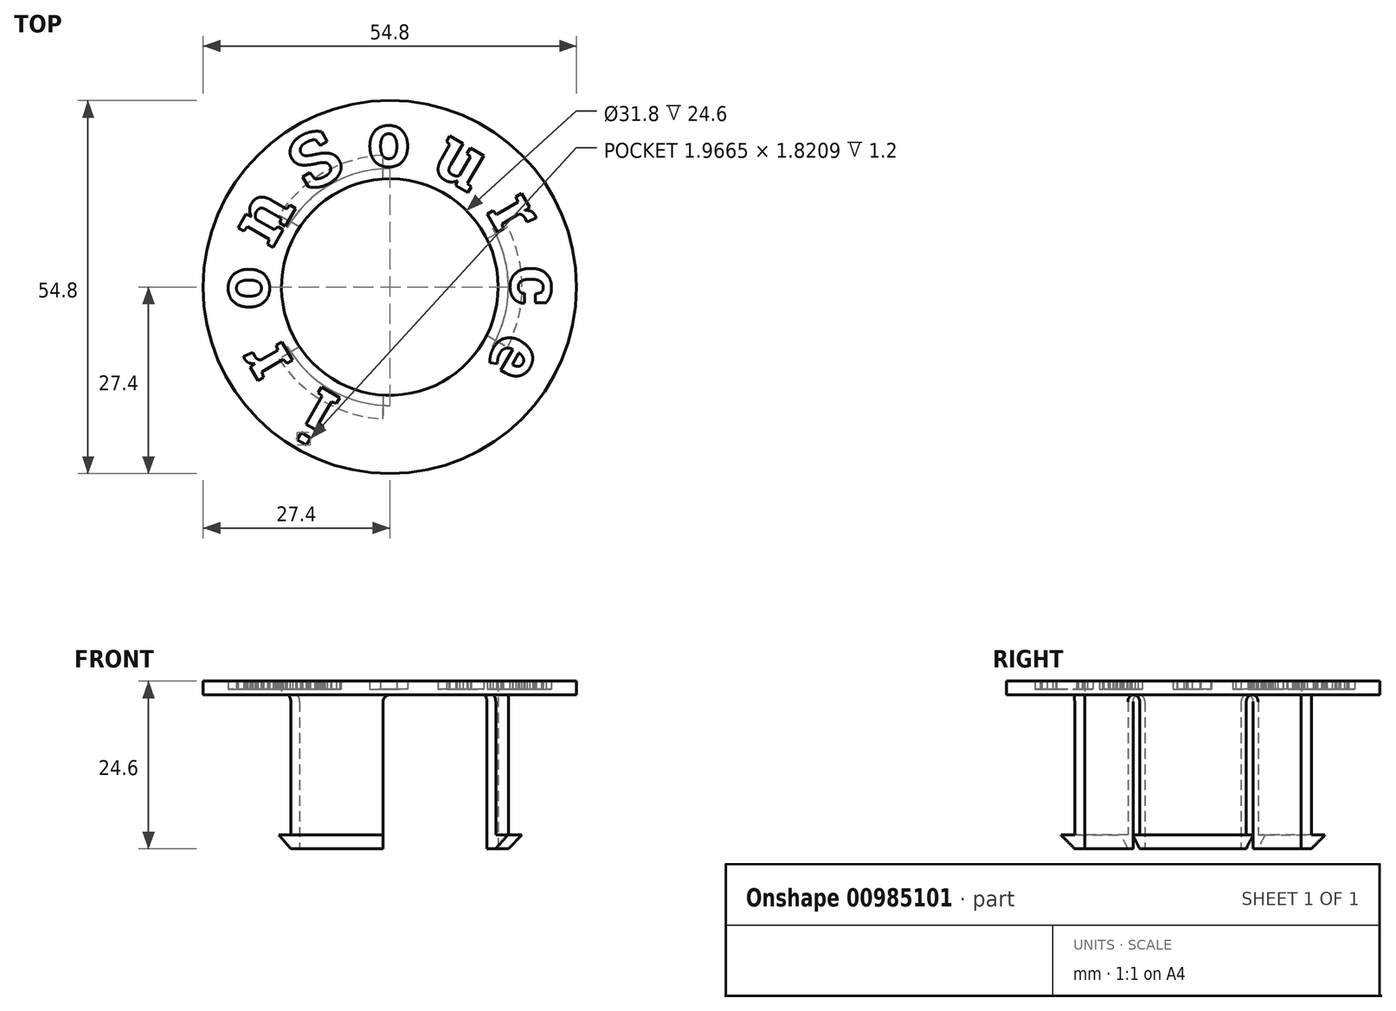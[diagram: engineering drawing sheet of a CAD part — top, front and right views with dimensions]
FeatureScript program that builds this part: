
annotation { "Feature Type Name" : "Feature", "Feature Type Description" : "" }
export const myFeature = defineFeature(function(context is Context, id is Id, definition is map)
    precondition{}
    {
        {
            var Q0;
            Q0=qCreatedBy(makeId("Top.planeOp"),FACE);
            var sketch = newSketch(context, id + "F0", { "sketchPlane" : qUnion([Q0])});
            skCircle(sketch, "E0", {"center": v(0, 0) * mm, "radius": 17.4 * mm});
            skCircle(sketch, "E1", {"center": v(0, 0) * mm, "radius": 15.9 * mm});
            skCircle(sketch, "E2", {"center": v(0, 0) * mm, "radius": 27.4 * mm});
            skLineSegment(sketch, "E3", {"start": v(0, 0) * mm, "end": v(0, 17.75) * mm, "construction": true});
            skText(sketch, "E4", { "text": "o", "fontName": "RobotoSlab-Bold.ttf"});
            skText(sketch, "E5", { "text": "u", "fontName": "RobotoSlab-Bold.ttf"});
            skText(sketch, "E6", { "text": "e", "fontName": "RobotoSlab-Bold.ttf"});
            skText(sketch, "E7", { "text": "i", "fontName": "RobotoSlab-Bold.ttf"});
            skText(sketch, "E8", { "text": "r", "fontName": "RobotoSlab-Bold.ttf"});
            skText(sketch, "E9", { "text": "c", "fontName": "RobotoSlab-Bold.ttf"});
            skText(sketch, "E10", { "text": "e", "fontName": "RobotoSlab-Bold.ttf"});
            skText(sketch, "E11", { "text": "o", "fontName": "RobotoSlab-Bold.ttf"});
            skText(sketch, "E12", { "text": "r", "fontName": "RobotoSlab-Bold.ttf"});
            skText(sketch, "E13", { "text": "n", "fontName": "RobotoSlab-Bold.ttf"});
            skLineSegment(sketch, "E14.2.0", {"start": v(0, 0) * mm, "end": v(-15.37, 8.88) * mm, "construction": true});
            skLineSegment(sketch, "E14.3.0", {"start": v(0, 0) * mm, "end": v(-17.75, 0) * mm, "construction": true});
            skLineSegment(sketch, "E14.4.0", {"start": v(0, 0) * mm, "end": v(-15.37, -8.88) * mm, "construction": true});
            skLineSegment(sketch, "E14.5.0", {"start": v(0, 0) * mm, "end": v(-8.88, -15.37) * mm, "construction": true});
            skLineSegment(sketch, "E14.6.0", {"start": v(0, 0) * mm, "end": v(0, -17.75) * mm, "construction": true});
            skLineSegment(sketch, "E14.7.0", {"start": v(0, 0) * mm, "end": v(8.87, -15.37) * mm, "construction": true});
            skLineSegment(sketch, "E14.8.0", {"start": v(0, 0) * mm, "end": v(15.37, -8.88) * mm, "construction": true});
            skLineSegment(sketch, "E14.9.0", {"start": v(0, 0) * mm, "end": v(17.75, 0) * mm, "construction": true});
            skLineSegment(sketch, "E14.10.0", {"start": v(0, 0) * mm, "end": v(15.37, 8.87) * mm, "construction": true});
            skLineSegment(sketch, "E14.11.0", {"start": v(0, 0) * mm, "end": v(8.88, 15.37) * mm, "construction": true});
            skText(sketch, "E15", { "text": "S", "fontName": "RobotoSlab-Bold.ttf"});
            skLineSegment(sketch, "E16", {"start": v(0, 0) * mm, "end": v(-8.88, 15.37) * mm, "construction": true});
            const initialGuessF0  = {"E4": [-0.00328, 0.01775, 1, 0, 0.008], "E5": [0.0057, 0.0172, 0.86603, -0.5, 0.008], "E6": [0.01692, -0.0062, -0.5, -0.86603, 0.008], "E7": [-0.0071, -0.0164, -0.86603, 0.5, 0.008], "E8": [-0.01407, -0.01114, -0.5, 0.86603, 0.008], "E9": [0.01775, 0.0031, 0, -1, 0.008], "E10": [0.01156, -0.01382, -0.86603, -0.5, 0.008], "E11": [-0.01775, -0.00328, 0, 1, 0.008], "E12": [0.01407, 0.01114, 0.5, -0.86603, 0.008], "E13": [-0.01726, 0.0056, 0.5, 0.86603, 0.008], "E15": [-0.01195, 0.0136, 0.86603, 0.5, 0.008]};
            skSetInitialGuess(sketch, initialGuessF0);
            skSolve(sketch);
        }
        {
            var Q0;
            Q0=makeQuery(id+"F0.imprint","IMPRINT",FACE,{"disambiguationData":[TD([[makeQuery(id+"F0.imprint","IMPRINT",EDGE,{"derivedFrom":sQuery(id+"F0.wireOp",EDGE,"E0")}),1.0]])]});
            var Q1;
            Q1=makeQuery(id+"F0.imprint","IMPRINT",FACE,{"disambiguationData":[TD([[makeQuery(id+"F0.imprint","IMPRINT",EDGE,{"derivedFrom":sQuery(id+"F0.wireOp",EDGE,"E4.sketch_text.stroke-0")}),-1.0]])]});
            var Q2;
            Q2=makeQuery(id+"F0.imprint","IMPRINT",FACE,{"disambiguationData":[TD([[makeQuery(id+"F0.imprint","IMPRINT",EDGE,{"derivedFrom":sQuery(id+"F0.wireOp",EDGE,"E7.sketch_text.stroke-0")}),-1.0]])]});
            var Q3;
            Q3=makeQuery(id+"F0.imprint","IMPRINT",FACE,{"disambiguationData":[TD([[makeQuery(id+"F0.imprint","IMPRINT",EDGE,{"derivedFrom":sQuery(id+"F0.wireOp",EDGE,"E11.sketch_text.stroke-10")}),1.0]])]});
            var Q4;
            Q4=makeQuery(id+"F0.imprint","IMPRINT",FACE,{"disambiguationData":[TD([[makeQuery(id+"F0.imprint","IMPRINT",EDGE,{"derivedFrom":sQuery(id+"F0.wireOp",EDGE,"E9.sketch_text.stroke-0")}),-1.0]])]});
            var Q5;
            Q5=makeQuery(id+"F0.imprint","IMPRINT",FACE,{"disambiguationData":[TD([[makeQuery(id+"F0.imprint","IMPRINT",EDGE,{"derivedFrom":sQuery(id+"F0.wireOp",EDGE,"E10.sketch_text.stroke-0")}),-1.0]])]});
            var Q6;
            Q6=makeQuery(id+"F0.imprint","IMPRINT",FACE,{"disambiguationData":[TD([[makeQuery(id+"F0.imprint","IMPRINT",EDGE,{"derivedFrom":sQuery(id+"F0.wireOp",EDGE,"E6.sketch_text.stroke-0")}),-1.0]])]});
            var Q7;
            Q7=makeQuery(id+"F0.imprint","IMPRINT",FACE,{"disambiguationData":[TD([[makeQuery(id+"F0.imprint","IMPRINT",EDGE,{"derivedFrom":sQuery(id+"F0.wireOp",EDGE,"E12.sketch_text.stroke-0")}),-1.0]])]});
            var Q8;
            Q8=makeQuery(id+"F0.imprint","IMPRINT",FACE,{"disambiguationData":[TD([[makeQuery(id+"F0.imprint","IMPRINT",EDGE,{"derivedFrom":sQuery(id+"F0.wireOp",EDGE,"E5.sketch_text.stroke-0")}),-1.0]])]});
            var Q9;
            Q9=makeQuery(id+"F0.imprint","IMPRINT",FACE,{"disambiguationData":[TD([[makeQuery(id+"F0.imprint","IMPRINT",EDGE,{"derivedFrom":sQuery(id+"F0.wireOp",EDGE,"E0")}),-1.0]])]});
            var Q10;
            Q10=makeQuery(id+"F0.imprint","IMPRINT",FACE,{"disambiguationData":[TD([[makeQuery(id+"F0.imprint","IMPRINT",EDGE,{"derivedFrom":sQuery(id+"F0.wireOp",EDGE,"E5.sketch_text.stroke-10")}),1.0]])]});
            var Q11;
            Q11=makeQuery(id+"F0.imprint","IMPRINT",FACE,{"disambiguationData":[TD([[makeQuery(id+"F0.imprint","IMPRINT",EDGE,{"derivedFrom":sQuery(id+"F0.wireOp",EDGE,"E13.sketch_text.stroke-0")}),-1.0]])]});
            var Q12;
            Q12=makeQuery(id+"F0.imprint","IMPRINT",FACE,{"disambiguationData":[TD([[makeQuery(id+"F0.imprint","IMPRINT",EDGE,{"derivedFrom":sQuery(id+"F0.wireOp",EDGE,"E8.sketch_text.stroke-0")}),-1.0]])]});
            var Q13;
            Q13=makeQuery(id+"F0.imprint","IMPRINT",FACE,{"disambiguationData":[TD([[makeQuery(id+"F0.imprint","IMPRINT",EDGE,{"derivedFrom":sQuery(id+"F0.wireOp",EDGE,"E11.sketch_text.stroke-0")}),-1.0]])]});
            var Q14;
            Q14=makeQuery(id+"F0.imprint","IMPRINT",FACE,{"disambiguationData":[TD([[makeQuery(id+"F0.imprint","IMPRINT",EDGE,{"derivedFrom":sQuery(id+"F0.wireOp",EDGE,"E7.sketch_text.stroke-10")}),-1.0]])]});
            var Q15;
            Q15=makeQuery(id+"F0.imprint","IMPRINT",FACE,{"disambiguationData":[TD([[makeQuery(id+"F0.imprint","IMPRINT",EDGE,{"derivedFrom":sQuery(id+"F0.wireOp",EDGE,"E10.sketch_text.stroke-17")}),1.0]])]});
            var Q16;
            Q16=makeQuery(id+"F0.imprint","IMPRINT",FACE,{"disambiguationData":[TD([[makeQuery(id+"F0.imprint","IMPRINT",EDGE,{"derivedFrom":sQuery(id+"F0.wireOp",EDGE,"E15.sketch_text.stroke-0")}),-1.0]])]});
            var Q17;
            Q17=makeQuery(id+"F0.imprint","IMPRINT",FACE,{"disambiguationData":[TD([[makeQuery(id+"F0.imprint","IMPRINT",EDGE,{"derivedFrom":sQuery(id+"F0.wireOp",EDGE,"E4.sketch_text.stroke-10")}),1.0]])]});
            var Q18;
            Q18=makeQuery(id+"F0.imprint","IMPRINT",FACE,{"disambiguationData":[TD([[makeQuery(id+"F0.imprint","IMPRINT",EDGE,{"derivedFrom":sQuery(id+"F0.wireOp",EDGE,"E6.sketch_text.stroke-17")}),1.0]])]});
            extrude(context, id + "F1", {"entities" : qUnion([Q0, Q1, Q2, Q3, Q4, Q5, Q6, Q7, Q8, Q9, Q10, Q11, Q12, Q13, Q14, Q15, Q16, Q17, Q18]), "depth" : 0.8 * mm, "offsetDistance" : 25 * mm});
        }
        {
            var Q0;
            Q0 = qSketchRegion(id + "F0", true);
            var Q1;
            Q1=makeQuery(id+"F0.imprint","IMPRINT",FACE,{"disambiguationData":[TD([[makeQuery(id+"F0.imprint","IMPRINT",EDGE,{"derivedFrom":sQuery(id+"F0.wireOp",EDGE,"E8.sketch_text.stroke-29")}),1.0]])]});
            var Q2;
            Q2=makeQuery(id+"F0.imprint","IMPRINT",FACE,{"disambiguationData":[TD([[makeQuery(id+"F0.imprint","IMPRINT",EDGE,{"derivedFrom":sQuery(id+"F0.wireOp",EDGE,"E11.sketch_text.stroke-10")}),1.0]])]});
            var Q3;
            Q3=makeQuery(id+"F0.imprint","IMPRINT",FACE,{"disambiguationData":[TD([[makeQuery(id+"F0.imprint","IMPRINT",EDGE,{"derivedFrom":sQuery(id+"F0.wireOp",EDGE,"E5.sketch_text.stroke-10")}),1.0]])]});
            var Q4;
            Q4=makeQuery(id+"F0.imprint","IMPRINT",FACE,{"disambiguationData":[TD([[makeQuery(id+"F0.imprint","IMPRINT",EDGE,{"derivedFrom":sQuery(id+"F0.wireOp",EDGE,"E9.sketch_text.stroke-29")}),1.0]])]});
            var Q5;
            Q5=makeQuery(id+"F0.imprint","IMPRINT",FACE,{"disambiguationData":[TD([[makeQuery(id+"F0.imprint","IMPRINT",EDGE,{"derivedFrom":sQuery(id+"F0.wireOp",EDGE,"E0")}),1.0]])]});
            var Q6;
            Q6=makeQuery(id+"F0.imprint","IMPRINT",FACE,{"disambiguationData":[TD([[makeQuery(id+"F0.imprint","IMPRINT",EDGE,{"derivedFrom":sQuery(id+"F0.wireOp",EDGE,"E10.sketch_text.stroke-17")}),1.0]])]});
            var Q7;
            Q7=makeQuery(id+"F0.imprint","IMPRINT",FACE,{"disambiguationData":[TD([[makeQuery(id+"F0.imprint","IMPRINT",EDGE,{"derivedFrom":sQuery(id+"F0.wireOp",EDGE,"E4.sketch_text.stroke-10")}),1.0]])]});
            var Q8;
            Q8=makeQuery(id+"F0.imprint","IMPRINT",FACE,{"disambiguationData":[TD([[makeQuery(id+"F0.imprint","IMPRINT",EDGE,{"derivedFrom":sQuery(id+"F0.wireOp",EDGE,"E6.sketch_text.stroke-17")}),1.0]])]});
            var Q9;
            Q9=makeQuery(id+"F0.imprint","IMPRINT",FACE,{"disambiguationData":[TD([[makeQuery(id+"F0.imprint","IMPRINT",EDGE,{"derivedFrom":sQuery(id+"F0.wireOp",EDGE,"E10.sketch_text.stroke-0")}),-1.0]])]});
            extrude(context, id + "F2", {"entities" : qUnion([Q0, Q1, Q2, Q3, Q4, Q5, Q6, Q7, Q8, Q9]), "operationType" : NewBodyOperationType.ADD, "depth" : 2 * mm, "offsetDistance" : 25 * mm});
        }
        {
            var Q0;
            Q0=makeQuery(id+"F0.imprint","IMPRINT",FACE,{"disambiguationData":[TD([[makeQuery(id+"F0.imprint","IMPRINT",EDGE,{"derivedFrom":sQuery(id+"F0.wireOp",EDGE,"E0")}),1.0]])]});
            extrude(context, id + "F3", {"entities" : qUnion([Q0]), "operationType" : NewBodyOperationType.ADD, "oppositeDirection" : true, "depth" : 22.6 * mm, "offsetDistance" : 25 * mm});
        }
        {
            var Q0;
            Q0=makeQuery(id+"F3.opExtrude","CAP_FACE",FACE,{"disambiguationData":[OSD([sQuery(id+"F0.wireOp",EDGE,"E0"),sQuery(id+"F0.wireOp",EDGE,"E1")])],"isStart":false});
            var sketch = newSketch(context, id + "F4", { "sketchPlane" : qUnion([Q0])});
            skLineSegment(sketch, "E17.bottom", {"start": v(1, 0) * mm, "end": v(-1, 0) * mm});
            skLineSegment(sketch, "E17.top", {"start": v(1, -20) * mm, "end": v(-1, -20) * mm});
            skLineSegment(sketch, "E17.left", {"start": v(1, 0) * mm, "end": v(1, -20) * mm});
            skLineSegment(sketch, "E17.right", {"start": v(-1, 0) * mm, "end": v(-1, -20) * mm});
            skLineSegment(sketch, "E18.1.0", {"start": v(0.5, 0.87) * mm, "end": v(-0.5, -0.87) * mm});
            skLineSegment(sketch, "E18.1.1", {"start": v(17.82, -9.13) * mm, "end": v(16.82, -10.87) * mm});
            skLineSegment(sketch, "E18.1.2", {"start": v(-0.5, -0.87) * mm, "end": v(16.82, -10.87) * mm});
            skLineSegment(sketch, "E18.1.3", {"start": v(0.5, 0.87) * mm, "end": v(17.82, -9.13) * mm});
            skLineSegment(sketch, "E18.2.0", {"start": v(-0.5, 0.87) * mm, "end": v(0.5, -0.87) * mm});
            skLineSegment(sketch, "E18.2.1", {"start": v(16.82, 10.87) * mm, "end": v(17.82, 9.13) * mm});
            skLineSegment(sketch, "E18.2.2", {"start": v(0.5, -0.87) * mm, "end": v(17.82, 9.13) * mm});
            skLineSegment(sketch, "E18.2.3", {"start": v(-0.5, 0.87) * mm, "end": v(16.82, 10.87) * mm});
            skLineSegment(sketch, "E18.3.0", {"start": v(-1, 0) * mm, "end": v(1, 0) * mm});
            skLineSegment(sketch, "E18.3.1", {"start": v(-1, 20) * mm, "end": v(1, 20) * mm});
            skLineSegment(sketch, "E18.3.2", {"start": v(1, 0) * mm, "end": v(1, 20) * mm});
            skLineSegment(sketch, "E18.3.3", {"start": v(-1, 0) * mm, "end": v(-1, 20) * mm});
            skLineSegment(sketch, "E18.4.0", {"start": v(-0.5, -0.87) * mm, "end": v(0.5, 0.87) * mm});
            skLineSegment(sketch, "E18.4.1", {"start": v(-17.82, 9.13) * mm, "end": v(-16.82, 10.87) * mm});
            skLineSegment(sketch, "E18.4.2", {"start": v(0.5, 0.87) * mm, "end": v(-16.82, 10.87) * mm});
            skLineSegment(sketch, "E18.4.3", {"start": v(-0.5, -0.87) * mm, "end": v(-17.82, 9.13) * mm});
            skLineSegment(sketch, "E18.5.0", {"start": v(0.5, -0.87) * mm, "end": v(-0.5, 0.87) * mm});
            skLineSegment(sketch, "E18.5.1", {"start": v(-16.82, -10.87) * mm, "end": v(-17.82, -9.13) * mm});
            skLineSegment(sketch, "E18.5.2", {"start": v(-0.5, 0.87) * mm, "end": v(-17.82, -9.13) * mm});
            skLineSegment(sketch, "E18.5.3", {"start": v(0.5, -0.87) * mm, "end": v(-16.82, -10.87) * mm});
            skPoint(sketch, "E18.center", {"position": v(0, 0) * mm});
            skCircle(sketch, "E19", {"center": v(0, 0) * mm, "radius": 19.4 * mm});
            skSolve(sketch);
        }
        {
            var Q0;
            {var subQ0=sQuery(id+"F4.wireOp",EDGE,"E18.1.2");var subQ1=makeQuery(id+"F3.opExtrude","CAP_EDGE",EDGE,{"disambiguationData":[OSD([sQuery(id+"F0.wireOp",EDGE,"E1")])],"isStart":false});var subQ2=makeQuery(id+"F4.imprint","INTERSECT",VERTEX,{"derivedFrom":[subQ1,subQ0]});Q0=makeQuery(id+"F4.imprint","IMPRINT",FACE,{"disambiguationData":[TD([[makeQuery(id+"F4.imprint","IMPRINT",EDGE,{"disambiguationData":[TD([[subQ2,-1.0]])],"derivedFrom":subQ0}),1.0]])]});}
            var Q1;
            {var subQ0=sQuery(id+"F4.wireOp",EDGE,"E17.left");var subQ1=makeQuery(id+"F3.opExtrude","CAP_EDGE",EDGE,{"disambiguationData":[OSD([sQuery(id+"F0.wireOp",EDGE,"E1")])],"isStart":false});var subQ2=makeQuery(id+"F4.imprint","INTERSECT",VERTEX,{"derivedFrom":[subQ1,subQ0]});Q1=makeQuery(id+"F4.imprint","IMPRINT",FACE,{"disambiguationData":[TD([[makeQuery(id+"F4.imprint","IMPRINT",EDGE,{"disambiguationData":[TD([[subQ2,-1.0]])],"derivedFrom":subQ0}),-1.0]])]});}
            var Q2;
            {var subQ0=sQuery(id+"F4.wireOp",EDGE,"E18.5.2");var subQ1=makeQuery(id+"F3.opExtrude","CAP_EDGE",EDGE,{"disambiguationData":[OSD([sQuery(id+"F0.wireOp",EDGE,"E1")])],"isStart":false});var subQ2=makeQuery(id+"F4.imprint","INTERSECT",VERTEX,{"derivedFrom":[subQ1,subQ0]});Q2=makeQuery(id+"F4.imprint","IMPRINT",FACE,{"disambiguationData":[TD([[makeQuery(id+"F4.imprint","IMPRINT",EDGE,{"disambiguationData":[TD([[subQ2,-1.0]])],"derivedFrom":subQ0}),1.0]])]});}
            var Q3;
            {var subQ0=sQuery(id+"F4.wireOp",EDGE,"E18.4.2");var subQ1=makeQuery(id+"F3.opExtrude","CAP_EDGE",EDGE,{"disambiguationData":[OSD([sQuery(id+"F0.wireOp",EDGE,"E1")])],"isStart":false});var subQ2=makeQuery(id+"F4.imprint","INTERSECT",VERTEX,{"derivedFrom":[subQ1,subQ0]});Q3=makeQuery(id+"F4.imprint","IMPRINT",FACE,{"disambiguationData":[TD([[makeQuery(id+"F4.imprint","IMPRINT",EDGE,{"disambiguationData":[TD([[subQ2,-1.0]])],"derivedFrom":subQ0}),1.0]])]});}
            var Q4;
            {var subQ0=sQuery(id+"F4.wireOp",EDGE,"E18.3.2");var subQ1=makeQuery(id+"F3.opExtrude","CAP_EDGE",EDGE,{"disambiguationData":[OSD([sQuery(id+"F0.wireOp",EDGE,"E1")])],"isStart":false});var subQ2=makeQuery(id+"F4.imprint","INTERSECT",VERTEX,{"derivedFrom":[subQ1,subQ0]});Q4=makeQuery(id+"F4.imprint","IMPRINT",FACE,{"disambiguationData":[TD([[makeQuery(id+"F4.imprint","IMPRINT",EDGE,{"disambiguationData":[TD([[subQ2,-1.0]])],"derivedFrom":subQ0}),1.0]])]});}
            var Q5;
            {var subQ0=sQuery(id+"F4.wireOp",EDGE,"E18.2.2");var subQ1=makeQuery(id+"F3.opExtrude","CAP_EDGE",EDGE,{"disambiguationData":[OSD([sQuery(id+"F0.wireOp",EDGE,"E1")])],"isStart":false});var subQ2=makeQuery(id+"F4.imprint","INTERSECT",VERTEX,{"derivedFrom":[subQ1,subQ0]});Q5=makeQuery(id+"F4.imprint","IMPRINT",FACE,{"disambiguationData":[TD([[makeQuery(id+"F4.imprint","IMPRINT",EDGE,{"disambiguationData":[TD([[subQ2,-1.0]])],"derivedFrom":subQ0}),1.0]])]});}
            var Q6;
            {var subQ0=sQuery(id+"F4.wireOp",EDGE,"E17.left");var subQ1=makeQuery(id+"F3.opExtrude","CAP_EDGE",EDGE,{"disambiguationData":[OSD([sQuery(id+"F0.wireOp",EDGE,"E1")])],"isStart":false});var subQ2=makeQuery(id+"F4.imprint","INTERSECT",VERTEX,{"derivedFrom":[subQ1,subQ0]});Q6=makeQuery(id+"F4.imprint","IMPRINT",FACE,{"disambiguationData":[TD([[makeQuery(id+"F4.imprint","IMPRINT",EDGE,{"disambiguationData":[TD([[subQ2,-1.0]])],"derivedFrom":subQ0}),1.0]])]});}
            var Q7;
            {var subQ0=sQuery(id+"F4.wireOp",EDGE,"E18.4.3");var subQ1=makeQuery(id+"F3.opExtrude","CAP_EDGE",EDGE,{"disambiguationData":[OSD([sQuery(id+"F0.wireOp",EDGE,"E1")])],"isStart":false});var subQ2=makeQuery(id+"F4.imprint","INTERSECT",VERTEX,{"derivedFrom":[subQ1,subQ0]});Q7=makeQuery(id+"F4.imprint","IMPRINT",FACE,{"disambiguationData":[TD([[makeQuery(id+"F4.imprint","IMPRINT",EDGE,{"disambiguationData":[TD([[subQ2,-1.0]])],"derivedFrom":subQ0}),1.0]])]});}
            var Q8;
            {var subQ0=sQuery(id+"F4.wireOp",EDGE,"E18.2.3");var subQ1=makeQuery(id+"F3.opExtrude","CAP_EDGE",EDGE,{"disambiguationData":[OSD([sQuery(id+"F0.wireOp",EDGE,"E1")])],"isStart":false});var subQ2=makeQuery(id+"F4.imprint","INTERSECT",VERTEX,{"derivedFrom":[subQ1,subQ0]});Q8=makeQuery(id+"F4.imprint","IMPRINT",FACE,{"disambiguationData":[TD([[makeQuery(id+"F4.imprint","IMPRINT",EDGE,{"disambiguationData":[TD([[subQ2,-1.0]])],"derivedFrom":subQ0}),1.0]])]});}
            var Q9;
            Q9=makeQuery(id+"F1.opExtrude","CAP_FACE",FACE,{"disambiguationData":[OSD([sQuery(id+"F0.wireOp",EDGE,"E1"),sQuery(id+"F0.wireOp",EDGE,"E2")])],"isStart":true});
            extrude(context, id + "F5", {"entities" : qUnion([Q0, Q1, Q2, Q3, Q4, Q5, Q6, Q7, Q8]), "operationType" : NewBodyOperationType.REMOVE, "endBound" : BoundingType.UP_TO_SURFACE, "oppositeDirection" : true, "depth" : 25 * mm, "endBoundEntityFace" : qUnion([Q9]), "offsetDistance" : 25 * mm});
        }
        {
            var Q0;
            {var subQ0=sQuery(id+"F4.wireOp",EDGE,"E19");var subQ1=sQuery(id+"F4.wireOp",EDGE,"E18.1.3");var subQ2=makeQuery(id+"F4.imprint","INTERSECT",VERTEX,{"derivedFrom":[subQ1,subQ0]});Q0=makeQuery(id+"F4.imprint","IMPRINT",FACE,{"disambiguationData":[TD([[makeQuery(id+"F4.imprint","IMPRINT",EDGE,{"disambiguationData":[TD([[subQ2,1.0]])],"derivedFrom":subQ1}),1.0]])]});}
            var Q1;
            {var subQ0=sQuery(id+"F4.wireOp",EDGE,"E19");var subQ1=sQuery(id+"F4.wireOp",EDGE,"E17.right");var subQ2=makeQuery(id+"F4.imprint","INTERSECT",VERTEX,{"derivedFrom":[subQ1,subQ0]});Q1=makeQuery(id+"F4.imprint","IMPRINT",FACE,{"disambiguationData":[TD([[makeQuery(id+"F4.imprint","IMPRINT",EDGE,{"disambiguationData":[TD([[subQ2,1.0]])],"derivedFrom":subQ1}),-1.0]])]});}
            var Q2;
            {var subQ0=sQuery(id+"F4.wireOp",EDGE,"E19");var subQ1=sQuery(id+"F4.wireOp",EDGE,"E18.3.3");var subQ2=makeQuery(id+"F4.imprint","INTERSECT",VERTEX,{"derivedFrom":[subQ1,subQ0]});Q2=makeQuery(id+"F4.imprint","IMPRINT",FACE,{"disambiguationData":[TD([[makeQuery(id+"F4.imprint","IMPRINT",EDGE,{"disambiguationData":[TD([[subQ2,1.0]])],"derivedFrom":subQ1}),1.0]])]});}
            extrude(context, id + "F6", {"entities" : qUnion([Q0, Q1, Q2]), "operationType" : NewBodyOperationType.ADD, "oppositeDirection" : true, "depth" : 2 * mm, "offsetDistance" : 25 * mm});
        }
        {
            var Q0;
            {var subQ0=sQuery(id+"F4.wireOp",EDGE,"E19");Q0=makeQuery(id+"F6.opExtrude","CAP_EDGE",EDGE,{"disambiguationData":[OSD([subQ0]),TDD([makeQuery(id+"F4.imprint","IMPRINT",EDGE,{"disambiguationData":[TD([[makeQuery(id+"F4.imprint","INTERSECT",VERTEX,{"derivedFrom":[sQuery(id+"F4.wireOp",EDGE,"E18.1.3"),subQ0]}),-1.0]])],"derivedFrom":subQ0})])],"isStart":true});}
            var Q1;
            {var subQ0=sQuery(id+"F4.wireOp",EDGE,"E19");Q1=makeQuery(id+"F6.opExtrude","CAP_EDGE",EDGE,{"disambiguationData":[OSD([subQ0]),TDD([makeQuery(id+"F4.imprint","IMPRINT",EDGE,{"disambiguationData":[TD([[makeQuery(id+"F4.imprint","INTERSECT",VERTEX,{"derivedFrom":[sQuery(id+"F4.wireOp",EDGE,"E18.2.3"),subQ0]}),-1.0]])],"derivedFrom":subQ0})])],"isStart":true});}
            var Q2;
            {var subQ0=sQuery(id+"F4.wireOp",EDGE,"E19");Q2=makeQuery(id+"F6.opExtrude","CAP_EDGE",EDGE,{"disambiguationData":[OSD([subQ0]),TDD([makeQuery(id+"F4.imprint","IMPRINT",EDGE,{"disambiguationData":[TD([[makeQuery(id+"F4.imprint","INTERSECT",VERTEX,{"derivedFrom":[sQuery(id+"F4.wireOp",EDGE,"E18.3.3"),subQ0]}),-1.0]])],"derivedFrom":subQ0})])],"isStart":true});}
            var Q3;
            {var subQ0=sQuery(id+"F4.wireOp",EDGE,"E19");Q3=makeQuery(id+"F6.opExtrude","CAP_EDGE",EDGE,{"disambiguationData":[OSD([subQ0]),TDD([makeQuery(id+"F4.imprint","IMPRINT",EDGE,{"disambiguationData":[TD([[makeQuery(id+"F4.imprint","INTERSECT",VERTEX,{"derivedFrom":[sQuery(id+"F4.wireOp",EDGE,"E17.right"),subQ0]}),1.0]])],"derivedFrom":subQ0})])],"isStart":true});}
            var Q4;
            {var subQ0=sQuery(id+"F4.wireOp",EDGE,"E19");Q4=makeQuery(id+"F6.opExtrude","CAP_EDGE",EDGE,{"disambiguationData":[OSD([subQ0]),TDD([makeQuery(id+"F4.imprint","IMPRINT",EDGE,{"disambiguationData":[TD([[makeQuery(id+"F4.imprint","INTERSECT",VERTEX,{"derivedFrom":[sQuery(id+"F4.wireOp",EDGE,"E17.left"),subQ0]}),-1.0]])],"derivedFrom":subQ0})])],"isStart":true});}
            var Q5;
            {var subQ0=sQuery(id+"F4.wireOp",EDGE,"E19");Q5=makeQuery(id+"F6.opExtrude","CAP_EDGE",EDGE,{"disambiguationData":[OSD([subQ0]),TDD([makeQuery(id+"F4.imprint","IMPRINT",EDGE,{"disambiguationData":[TD([[makeQuery(id+"F4.imprint","INTERSECT",VERTEX,{"derivedFrom":[sQuery(id+"F4.wireOp",EDGE,"E18.4.3"),subQ0]}),-1.0]])],"derivedFrom":subQ0})])],"isStart":true});}
            chamfer(context, id + "F7", {"entities" : qUnion([Q0, Q1, Q2, Q3, Q4, Q5]), "width" : 2 * mm, "tangentPropagation" : true});
        }
        {
            var Q0;
            {var subQ0=sQuery(id+"F4.wireOp",EDGE,"E17.right");var subQ2=sQuery(id+"F0.wireOp",EDGE,"E0");Q0=makeQuery(id+"F5.boolean.opBoolean","SPLIT",EDGE,{"disambiguationData":[TD([makeQuery(id+"F5.opExtrude","SWEPT_FACE",FACE,{"disambiguationData":[OSD([subQ0])]})])],"derivedFrom":makeQuery(id+"F3.opExtrude","CAP_EDGE",EDGE,{"disambiguationData":[OSD([subQ2])],"isStart":true})});}
            var Q1;
            {var subQ1=sQuery(id+"F0.wireOp",EDGE,"E0");var subQ2=sQuery(id+"F4.wireOp",EDGE,"E18.3.3");Q1=makeQuery(id+"F5.boolean.opBoolean","SPLIT",EDGE,{"disambiguationData":[TD([makeQuery(id+"F5.opExtrude","SWEPT_FACE",FACE,{"disambiguationData":[OSD([subQ2])]})])],"derivedFrom":makeQuery(id+"F3.opExtrude","CAP_EDGE",EDGE,{"disambiguationData":[OSD([subQ1])],"isStart":true})});}
            var Q2;
            {var subQ0=sQuery(id+"F4.wireOp",EDGE,"E18.1.3");var subQ2=sQuery(id+"F0.wireOp",EDGE,"E0");Q2=makeQuery(id+"F5.boolean.opBoolean","SPLIT",EDGE,{"disambiguationData":[TD([makeQuery(id+"F5.opExtrude","SWEPT_FACE",FACE,{"disambiguationData":[OSD([subQ0])]})])],"derivedFrom":makeQuery(id+"F3.opExtrude","CAP_EDGE",EDGE,{"disambiguationData":[OSD([subQ2])],"isStart":true})});}
            var Q3;
            Q3=makeQuery(id+"F5.boolean.opBoolean","COPY",EDGE,{"derivedFrom":makeQuery(id+"F5.opExtrude","CAP_EDGE",EDGE,{"disambiguationData":[OSD([sQuery(id+"F4.wireOp",EDGE,"E18.2.2")])],"isStart":false})});
            var Q4;
            Q4=makeQuery(id+"F5.boolean.opBoolean","COPY",EDGE,{"derivedFrom":makeQuery(id+"F5.opExtrude","CAP_EDGE",EDGE,{"disambiguationData":[OSD([sQuery(id+"F4.wireOp",EDGE,"E18.3.3")])],"isStart":false})});
            var Q5;
            Q5=makeQuery(id+"F5.boolean.opBoolean","COPY",EDGE,{"derivedFrom":makeQuery(id+"F5.opExtrude","CAP_EDGE",EDGE,{"disambiguationData":[OSD([sQuery(id+"F4.wireOp",EDGE,"E18.1.3")])],"isStart":false})});
            var Q6;
            Q6=makeQuery(id+"F5.boolean.opBoolean","COPY",EDGE,{"derivedFrom":makeQuery(id+"F5.opExtrude","CAP_EDGE",EDGE,{"disambiguationData":[OSD([sQuery(id+"F4.wireOp",EDGE,"E17.right")])],"isStart":false})});
            var Q7;
            Q7=makeQuery(id+"F5.boolean.opBoolean","COPY",EDGE,{"derivedFrom":makeQuery(id+"F5.opExtrude","CAP_EDGE",EDGE,{"disambiguationData":[OSD([sQuery(id+"F4.wireOp",EDGE,"E18.5.3")])],"isStart":false})});
            var Q8;
            Q8=makeQuery(id+"F5.boolean.opBoolean","COPY",EDGE,{"derivedFrom":makeQuery(id+"F5.opExtrude","CAP_EDGE",EDGE,{"disambiguationData":[OSD([sQuery(id+"F4.wireOp",EDGE,"E18.4.2")])],"isStart":false})});
            fillet(context, id + "F8", {"entities" : qUnion([Q0, Q1, Q2, Q3, Q4, Q5, Q6, Q7, Q8]), "radius" : 1 * mm, "tangentPropagation" : true, "allowEdgeOverflow" : false});
        }
    });
